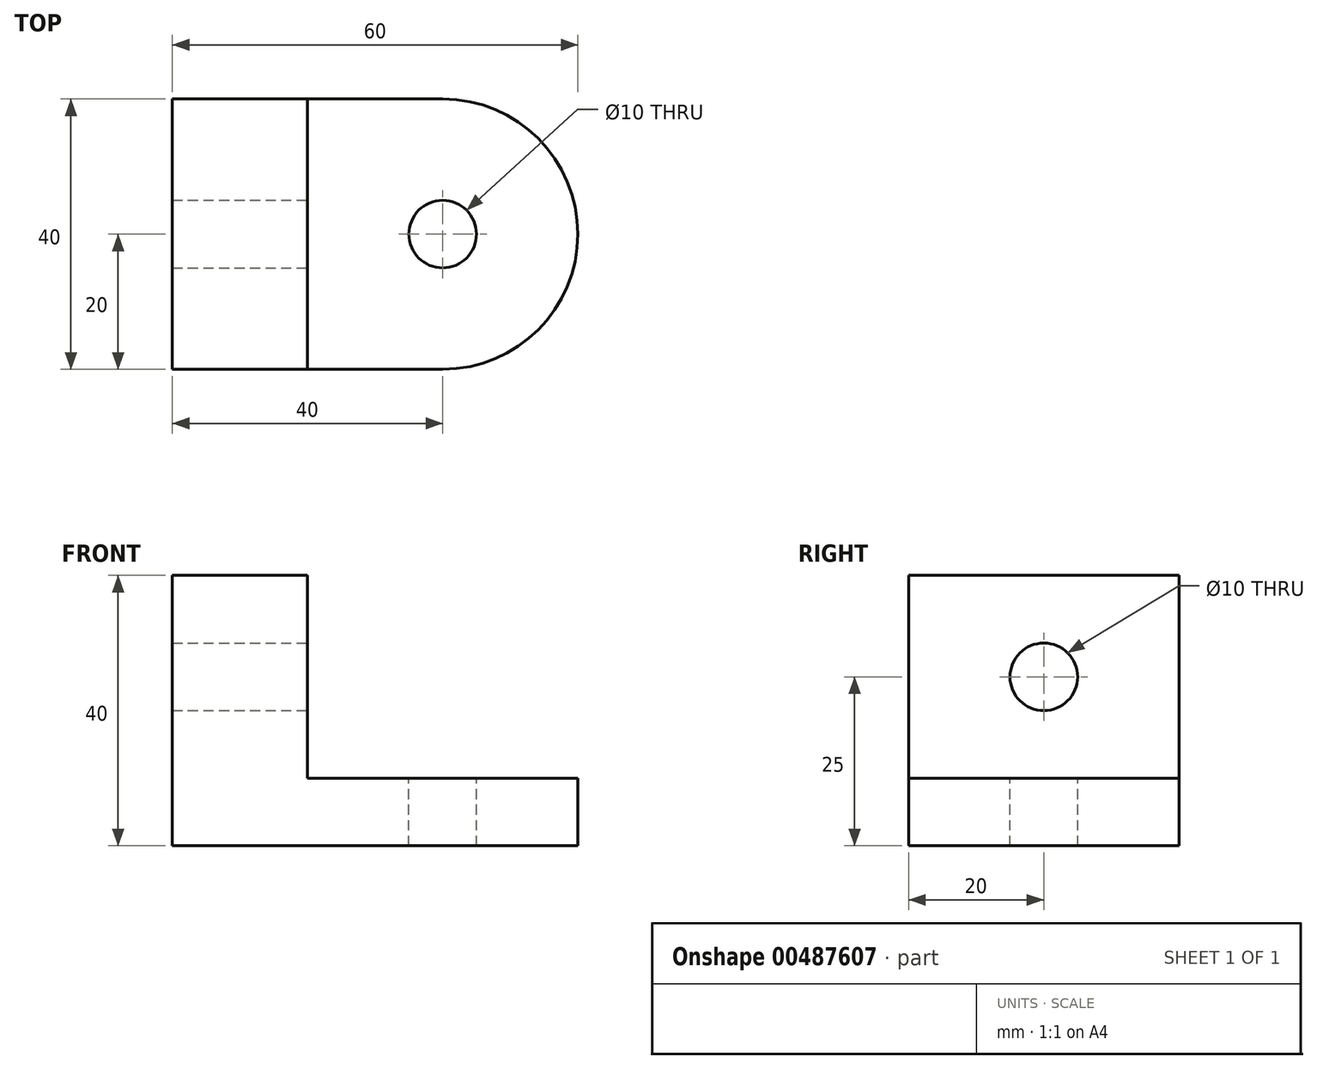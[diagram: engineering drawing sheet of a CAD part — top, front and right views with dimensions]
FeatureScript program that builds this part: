
annotation { "Feature Type Name" : "Feature", "Feature Type Description" : "" }
export const myFeature = defineFeature(function(context is Context, id is Id, definition is map)
    precondition{}
    {
        {
            var Q0;
            Q0=qCreatedBy(makeId("Front.planeOp"),FACE);
            var sketch = newSketch(context, id + "F0", { "sketchPlane" : qUnion([Q0])});
            skLineSegment(sketch, "E0", {"start": v(0, 0) * mm, "end": v(0, 20) * mm});
            skLineSegment(sketch, "E1", {"start": v(0, -20) * mm, "end": v(-20, -20) * mm});
            skLineSegment(sketch, "E2", {"start": v(-20, -20) * mm, "end": v(-20, 20) * mm});
            skLineSegment(sketch, "E3", {"start": v(-20, 20) * mm, "end": v(0, 20) * mm});
            skLineSegment(sketch, "E4", {"start": v(0, -20) * mm, "end": v(40, -20) * mm});
            skLineSegment(sketch, "E5", {"start": v(40, -20) * mm, "end": v(40, -10) * mm});
            skLineSegment(sketch, "E6", {"start": v(0, -10) * mm, "end": v(0, 0) * mm});
            skLineSegment(sketch, "E7", {"start": v(40, -10) * mm, "end": v(0, -10) * mm});
            skSolve(sketch);
        }
        {
            var Q0;
            Q0=makeQuery(id+"F0.imprint","IMPRINT",FACE,{"disambiguationData":[TD([[makeQuery(id+"F0.imprint","IMPRINT",EDGE,{"derivedFrom":sQuery(id+"F0.wireOp",EDGE,"E0")}),1.0]])]});
            extrude(context, id + "F1", {"entities" : qUnion([Q0]), "depth" : 40 * mm});
        }
        {
            var Q0;
            Q0=makeQuery(id+"F1.opExtrude","CAP_EDGE",EDGE,{"disambiguationData":[OSD([sQuery(id+"F0.wireOp",EDGE,"E5")])],"isStart":false});
            var Q1;
            Q1=makeQuery(id+"F1.opExtrude","CAP_EDGE",EDGE,{"disambiguationData":[OSD([sQuery(id+"F0.wireOp",EDGE,"E5")])],"isStart":true});
            fillet(context, id + "F2", {"entities" : qUnion([Q0, Q1]), "radius" : 20 * mm, "tangentPropagation" : true, "allowEdgeOverflow" : false});
        }
        {
            var Q0;
            Q0=makeQuery(id+"F1.opExtrude","SWEPT_FACE",FACE,{"disambiguationData":[OSD([sQuery(id+"F0.wireOp",EDGE,"E7")])]});
            var sketch = newSketch(context, id + "F3", { "sketchPlane" : qUnion([Q0])});
            skCircle(sketch, "E8", {"center": v(20, -20) * mm, "radius": 5 * mm});
            skSolve(sketch);
        }
        {
            var Q0;
            Q0=qSketchRegion(id+"F3",true);
            extrude(context, id + "F4", {"entities" : qUnion([Q0]), "operationType" : NewBodyOperationType.REMOVE, "oppositeDirection" : true, "depth" : 25 * mm});
        }
        {
            var Q0;
            Q0=makeQuery(id+"F1.opExtrude","SWEPT_FACE",FACE,{"disambiguationData":[OSD([sQuery(id+"F0.wireOp",EDGE,"E0"),sQuery(id+"F0.wireOp",EDGE,"E6")])]});
            var sketch = newSketch(context, id + "F5", { "sketchPlane" : qUnion([Q0])});
            skCircle(sketch, "E9", {"center": v(-20, 5) * mm, "radius": 5 * mm});
            skSolve(sketch);
        }
        {
            var Q0;
            Q0=makeQuery(id+"F5.imprint","IMPRINT",FACE,{"disambiguationData":[TD([[makeQuery(id+"F5.imprint","IMPRINT",EDGE,{"derivedFrom":sQuery(id+"F5.wireOp",EDGE,"E9")}),1.0]])]});
            extrude(context, id + "F6", {"entities" : qUnion([Q0]), "operationType" : NewBodyOperationType.REMOVE, "oppositeDirection" : true, "depth" : 25 * mm});
        }
    });
